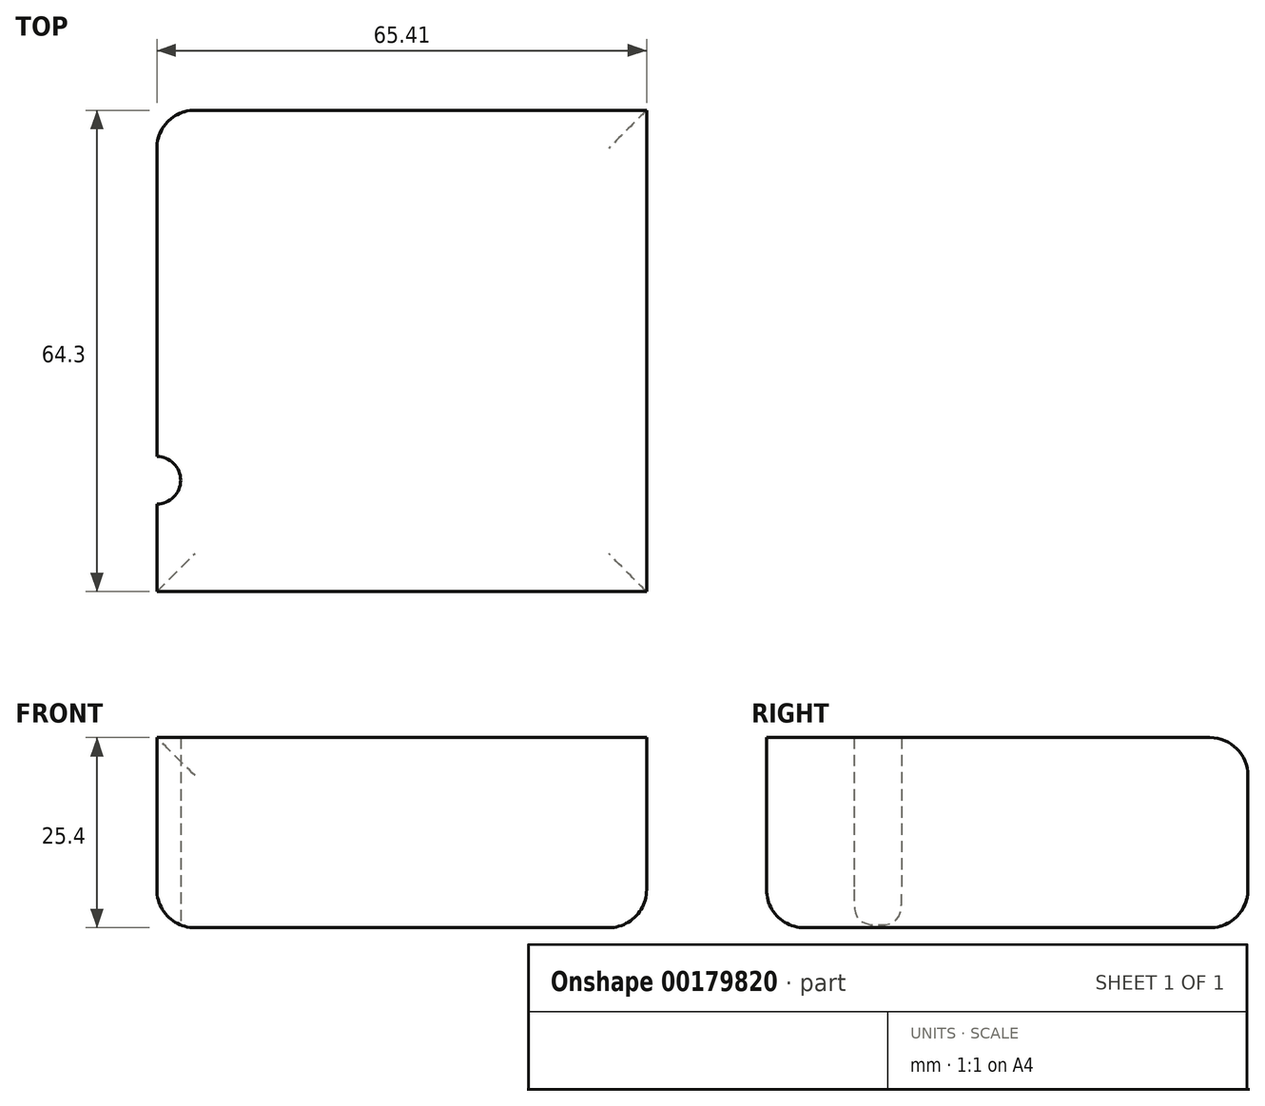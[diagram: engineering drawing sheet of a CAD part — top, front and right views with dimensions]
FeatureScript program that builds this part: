
annotation { "Feature Type Name" : "Feature", "Feature Type Description" : "" }
export const myFeature = defineFeature(function(context is Context, id is Id, definition is map)
    precondition{}
    {
        {
            var Q0;
            Q0=qCreatedBy(makeId("Top.planeOp"),FACE);
            var sketch = newSketch(context, id + "F0", { "sketchPlane" : qUnion([Q0])});
            skLineSegment(sketch, "E0.bottom", {"start": v(-21.8, 21.43) * mm, "end": v(43.6, 21.43) * mm});
            skLineSegment(sketch, "E0.top", {"start": v(-21.8, -42.87) * mm, "end": v(43.6, -42.87) * mm});
            skLineSegment(sketch, "E0.left", {"start": v(-21.8, 21.43) * mm, "end": v(-21.8, -42.87) * mm});
            skLineSegment(sketch, "E0.right", {"start": v(43.6, 21.43) * mm, "end": v(43.6, -42.87) * mm});
            skSolve(sketch);
        }
        {
            var Q0;
            Q0 = qSketchRegion(id + "F0", true);
            extrude(context, id + "F1", {"entities" : qUnion([Q0]), "depth" : 25.4 * mm});
        }
        {
            var Q0;
            Q0=makeQuery(id+"F1.opExtrude","CAP_FACE",FACE,{"disambiguationData":[OSD([sQuery(id+"F0.wireOp",EDGE,"E0.bottom"),sQuery(id+"F0.wireOp",EDGE,"E0.top"),sQuery(id+"F0.wireOp",EDGE,"E0.left"),sQuery(id+"F0.wireOp",EDGE,"E0.right")])],"isStart":true});
            var sketch = newSketch(context, id + "F2", { "sketchPlane" : qUnion([Q0])});
            skLineSegment(sketch, "E1.bottom", {"start": v(-21.8, 28) * mm, "end": v(26.2, 28) * mm});
            skLineSegment(sketch, "E1.top", {"start": v(-21.8, -11.73) * mm, "end": v(26.2, -11.73) * mm});
            skLineSegment(sketch, "E1.left", {"start": v(-21.8, 28) * mm, "end": v(-21.8, -11.73) * mm});
            skLineSegment(sketch, "E1.right", {"start": v(26.2, 28) * mm, "end": v(26.2, -11.73) * mm});
            skSolve(sketch);
        }
        {
            var Q0;
            Q0=makeQuery(id+"F1.opExtrude","CAP_EDGE",EDGE,{"disambiguationData":[OSD([sQuery(id+"F0.wireOp",EDGE,"E0.bottom")])],"isStart":false});
            var Q1;
            Q1=makeQuery(id+"F1.opExtrude","SWEPT_EDGE",EDGE,{"disambiguationData":[OSD([sQuery(id+"F0.wireOp",EDGE,"E0.bottom"),sQuery(id+"F0.wireOp",EDGE,"E0.left")])]});
            var Q2;
            Q2=makeQuery(id+"F1.opExtrude","CAP_FACE",FACE,{"disambiguationData":[OSD([sQuery(id+"F0.wireOp",EDGE,"E0.bottom"),sQuery(id+"F0.wireOp",EDGE,"E0.top"),sQuery(id+"F0.wireOp",EDGE,"E0.left"),sQuery(id+"F0.wireOp",EDGE,"E0.right")])],"isStart":true});
            fillet(context, id + "F3", {"entities" : qUnion([Q0, Q1, Q2]), "radius" : 5.08 * mm, "tangentPropagation" : true, "allowEdgeOverflow" : false});
        }
        {
            var Q0;
            Q0=sQuery(id+"F2.wireOp",VERTEX,"E1.left.start");
            var Q1;
            Q1=makeQuery(id+"F1.opExtrude","SWEPT_BODY",BODY,{"disambiguationData":[OSD([sQuery(id+"F0.wireOp",EDGE,"E0.bottom"),sQuery(id+"F0.wireOp",EDGE,"E0.top"),sQuery(id+"F0.wireOp",EDGE,"E0.left"),sQuery(id+"F0.wireOp",EDGE,"E0.right")])]});
            hole(context, id + "F4", {"style" : HoleStyle.SIMPLE, "endStyle" : HoleEndStyle.THROUGH, "holeDiameter" : 6.35 * mm, "locations" : qUnion([Q0]), "scope" : qUnion([Q1]), "isTappedThrough" : true});
        }
    });
